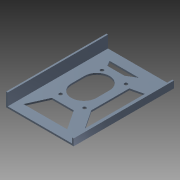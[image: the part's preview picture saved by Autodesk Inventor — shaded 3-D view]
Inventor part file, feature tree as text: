
AUTODESK INVENTOR PART (.ipt)
format: ipt  version: 2013 (Build 170138000, 138)  size: 169,472 bytes
history: native  units: mm
features: sketch x5, extrude x4, other x1, hole x1
ambient origin geometry x1: Origin
feature tree (11):
  other  "ソリッド1"
  extrude  "押し出し1"  Depth=92.0mm
  hole  "穴1"  [1 undecoded]
  extrude  "押し出し3"  Depth=62.0mm
  extrude  "押し出し5"  Depth=31.0mm
  extrude  "押し出し6"  Depth=1.5mm TaperAngle=0.0deg
  sketch  "スケッチ1"
  sketch  "スケッチ3"
  sketch  "スケッチ4"
  sketch  "スケッチ6"
  sketch  "スケッチ7"
note: 1 required parameter value undecoded (feature->parameter linkage not recoverable at this tier; creation-order binding heuristic only, values carry confidence <= 0.55)
